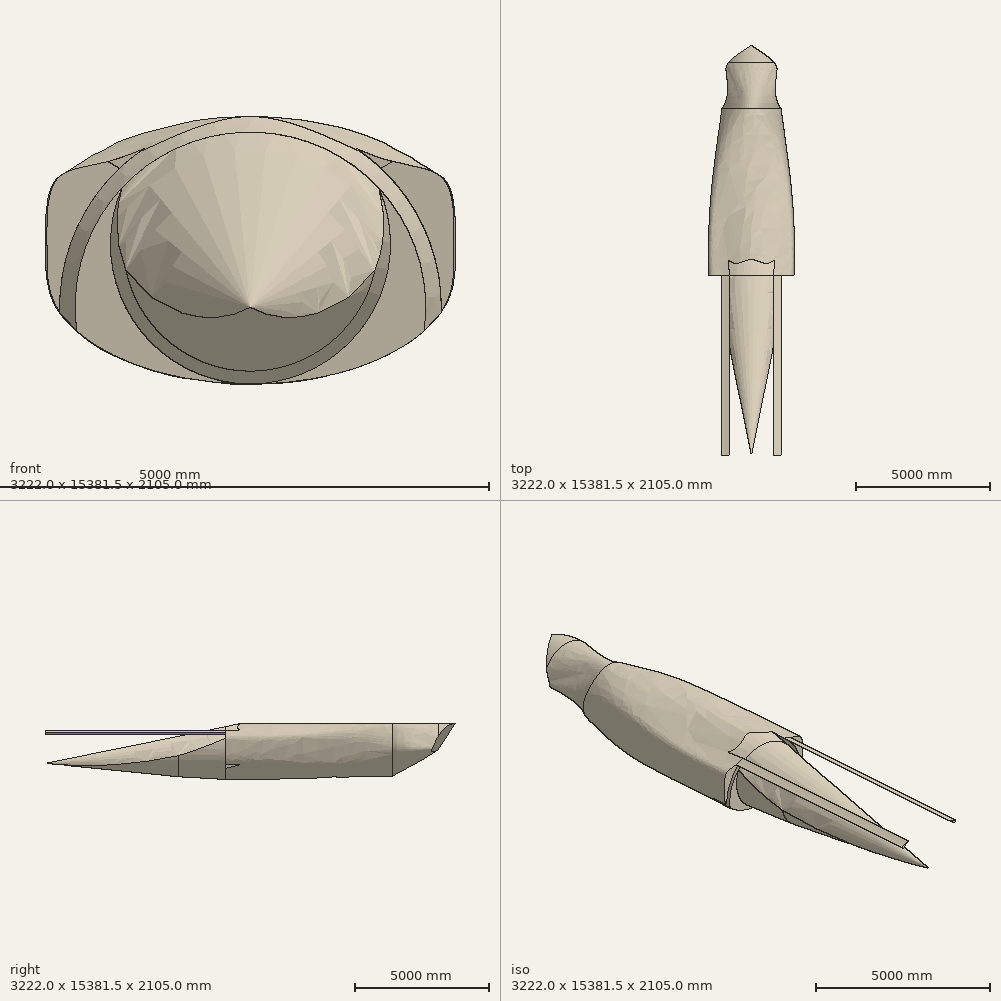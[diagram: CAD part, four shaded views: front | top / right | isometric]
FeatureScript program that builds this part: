
annotation { "Feature Type Name" : "Feature", "Feature Type Description" : "" }
export const myFeature = defineFeature(function(context is Context, id is Id, definition is map)
    precondition{}
    {
        {
            var Q0;
            Q0=qCreatedBy(makeId("Front.planeOp"),FACE);
            cPlane(context, id + "F0", {"entities" : qUnion([Q0]), "cplaneType" : CPlaneType.OFFSET, "offset" : 1750 * mm, "width" : 152.4 * mm, "height" : 152.4 * mm});
        }
        {
            var Q0;
            Q0=qCreatedBy(id+"F0.planeOp",FACE);
            var sketch = newSketch(context, id + "F1", { "sketchPlane" : qUnion([Q0])});
            skPoint(sketch, "E0.middle", {"position": v(0, 0) * mm});
            skFitSpline(sketch, "E1", {"points": [v(0, 1000) * mm, v(1060, 662.5) * mm, v(1517.6, 506.84) * mm, v(1600, 0) * mm, v(1517.6, -506.84) * mm, v(750, -1000) * mm, v(-750, -1000) * mm, v(-1517.6, -506.84) * mm, v(-1600, 0) * mm, v(-1517.6, 506.84) * mm, v(-1060, 662.5) * mm, v(0, 1000) * mm]});
            skSolve(sketch);
        }
        {
            var Q0;
            Q0=qCreatedBy(makeId("Front.planeOp"),FACE);
            var sketch = newSketch(context, id + "F2", { "sketchPlane" : qUnion([Q0])});
            skPoint(sketch, "E2.middle", {"position": v(0, 0) * mm});
            skFitSpline(sketch, "E3", {"points": [v(0, 1000) * mm, v(1060, 662.5) * mm, v(1517.6, 506.84) * mm, v(1600, 0) * mm, v(1517.6, -506.84) * mm, v(750, -1000) * mm, v(-750, -1000) * mm, v(-1517.6, -506.84) * mm, v(-1600, 0) * mm, v(-1517.6, 506.84) * mm, v(-1060, 662.5) * mm, v(0, 1000) * mm]});
            skSolve(sketch);
        }
        {
            var Q0;
            Q0=qCreatedBy(makeId("Front.planeOp"),FACE);
            cPlane(context, id + "F3", {"entities" : qUnion([Q0]), "cplaneType" : CPlaneType.OFFSET, "offset" : 3500 * mm, "oppositeDirection" : true, "width" : 150 * mm, "height" : 150 * mm});
        }
        {
            var Q0;
            Q0=qCreatedBy(id+"F3.planeOp",FACE);
            var sketch = newSketch(context, id + "F4", { "sketchPlane" : qUnion([Q0])});
            skPoint(sketch, "E4.middle", {"position": v(0, 0) * mm});
            skFitSpline(sketch, "E5", {"points": [v(0, 1000) * mm, v(1060, 662.5) * mm, v(1250, 0) * mm, v(1060, -662.5) * mm, v(0, -1000) * mm, v(-1060, -662.5) * mm, v(-1250, 0) * mm, v(-1060, 662.5) * mm, v(0, 1000) * mm]});
            skSolve(sketch);
        }
        {
            var Q0;
            Q0=qCreatedBy(makeId("Front.planeOp"),FACE);
            cPlane(context, id + "F5", {"entities" : qUnion([Q0]), "cplaneType" : CPlaneType.OFFSET, "offset" : 4500 * mm, "oppositeDirection" : true, "width" : 150 * mm, "height" : 150 * mm});
        }
        {
            var Q0;
            Q0=qCreatedBy(id+"F5.planeOp",FACE);
            var sketch = newSketch(context, id + "F6", { "sketchPlane" : qUnion([Q0])});
            skPoint(sketch, "E6.middle", {"position": v(0, 0) * mm});
            skFitSpline(sketch, "E7", {"points": [v(0, 1000) * mm, v(848, 530) * mm, v(1108.5, 0) * mm, v(848, -530) * mm, v(0, -1000) * mm, v(-848, -530) * mm, v(-1108.5, 0) * mm, v(-848, 530) * mm, v(0, 1000) * mm]});
            skSolve(sketch);
        }
        {
            var Q0;
            Q0=qCreatedBy(makeId("Front.planeOp"),FACE);
            cPlane(context, id + "F7", {"entities" : qUnion([Q0]), "cplaneType" : CPlaneType.OFFSET, "offset" : 6232.05 * mm, "oppositeDirection" : true, "width" : 150 * mm, "height" : 150 * mm});
        }
        {
            var Q0;
            Q0=qCreatedBy(id+"F7.planeOp",FACE);
            var sketch = newSketch(context, id + "F8", { "sketchPlane" : qUnion([Q0])});
            skArc(sketch, "E8", {"start": v(998.61, 52.63) * mm, "mid": v(0, 1000) * mm, "end": v(-998.61, 52.63) * mm});
            skLineSegment(sketch, "E9", {"start": v(0, 0) * mm, "end": v(-948.68, 0) * mm});
            skLineSegment(sketch, "E10", {"start": v(0, 0) * mm, "end": v(948.68, 0) * mm});
            skPoint(sketch, "E11.visualSharp", {"position": v(-1000, 0) * mm});
            skArc(sketch, "E11.filletArc", {"start": v(-998.61, 52.63) * mm, "mid": v(-984.96, 15.59) * mm, "end": v(-948.68, 0) * mm});
            skPoint(sketch, "E12.visualSharp", {"position": v(1000, 0) * mm});
            skArc(sketch, "E12.filletArc", {"start": v(948.68, 0) * mm, "mid": v(984.96, 15.59) * mm, "end": v(998.61, 52.63) * mm});
            skSolve(sketch);
        }
        {
            var Q0;
            Q0=sQuery(id+"F8.wireOp",EDGE,"E9");
            var Q1;
            Q1=sQuery(id+"F6.wireOp",VERTEX,"E7.6.internal");
            cPlane(context, id + "F9", {"entities" : qUnion([Q0, Q1]), "cplaneType" : CPlaneType.LINE_ANGLE, "offset" : 25 * mm, "angle" : 0 * degree, "width" : 150 * mm, "height" : 150 * mm});
        }
        {
            var Q0;
            Q0=qCreatedBy(id+"F9.planeOp",FACE);
            var sketch = newSketch(context, id + "F10", { "sketchPlane" : qUnion([Q0])});
            skFitSpline(sketch, "E13", {"points": [v(-1108.5, 4500) * mm, v(-948.68, 6232.05) * mm], "startDerivative": vector(1200, 1755) * mm, "endDerivative": vector(158.07, 1422.55) * mm});
            skFitSpline(sketch, "E14", {"points": [v(1108.5, 4500) * mm, v(948.68, 6232.05) * mm], "startDerivative": vector(-1200, 1755) * mm, "endDerivative": vector(-158.07, 1422.55) * mm});
            skSolve(sketch);
        }
        {
            var Q0;
            Q0=makeQuery(id+"F1.imprint","IMPRINT",FACE,{"disambiguationData":[TD([[makeQuery(id+"F1.imprint","IMPRINT",EDGE,{"derivedFrom":sQuery(id+"F1.wireOp",EDGE,"E1")}),-1.0]])]});
            var Q1;
            Q1=makeQuery(id+"F2.imprint","IMPRINT",FACE,{"disambiguationData":[TD([[makeQuery(id+"F2.imprint","IMPRINT",EDGE,{"derivedFrom":sQuery(id+"F2.wireOp",EDGE,"E3")}),-1.0]])]});
            var Q2;
            Q2=makeQuery(id+"F4.imprint","IMPRINT",FACE,{"disambiguationData":[TD([[makeQuery(id+"F4.imprint","IMPRINT",EDGE,{"derivedFrom":sQuery(id+"F4.wireOp",EDGE,"E5")}),-1.0]])]});
            var Q3;
            Q3=makeQuery(id+"F6.imprint","IMPRINT",FACE,{"disambiguationData":[TD([[makeQuery(id+"F6.imprint","IMPRINT",EDGE,{"derivedFrom":sQuery(id+"F6.wireOp",EDGE,"E7")}),-1.0]])]});
            loft(context, id + "F11", {"sheetProfilesArray" : [{ "sheetProfileEntities" : qUnion([Q0]) }, { "sheetProfileEntities" : qUnion([Q1]) }, { "sheetProfileEntities" : qUnion([Q2]) }, { "sheetProfileEntities" : qUnion([Q3]) }]});
        }
        {
            var Q1;
            Q1=makeQuery(id+"F6.imprint","IMPRINT",FACE,{"disambiguationData":[TD([[makeQuery(id+"F6.imprint","IMPRINT",EDGE,{"derivedFrom":sQuery(id+"F6.wireOp",EDGE,"E7")}),-1.0]])]});
            var Q2;
            Q2=makeQuery(id+"F8.imprint","IMPRINT",FACE,{"disambiguationData":[TD([[makeQuery(id+"F8.imprint","IMPRINT",EDGE,{"derivedFrom":sQuery(id+"F8.wireOp",EDGE,"E8")}),1.0]])]});
            var Q3;
            Q3=sQuery(id+"F10.wireOp",EDGE,"E13");
            var Q4;
            Q4=sQuery(id+"F10.wireOp",EDGE,"E14");
            loft(context, id + "F12", {"operationType" : NewBodyOperationType.ADD, "addGuides" : true, "sheetProfilesArray" : [{ "sheetProfileEntities" : qUnion([Q1]) }, { "sheetProfileEntities" : qUnion([Q2]) }], "guidesArray" : [{ "guideEntities" : qUnion([Q3]), "guideDerivativeType" : LoftGuideDerivativeType.DEFAULT, "guideDerivativeMagnitude" : 1 }, { "guideEntities" : qUnion([Q4]), "guideDerivativeType" : LoftGuideDerivativeType.DEFAULT, "guideDerivativeMagnitude" : 1 }]});
        }
        {
            var Q0;
            Q0=qSketchRegion(id+"F1",true);
            extrude(context, id + "F13", {"entities" : qUnion([Q0]), "depth" : 6750 * mm});
        }
        {
            var Q0;
            Q0=qCreatedBy(makeId("Right.planeOp"),FACE);
            var sketch = newSketch(context, id + "F14", { "sketchPlane" : qUnion([Q0])});
            skLineSegment(sketch, "E15", {"start": v(0, 0) * mm, "end": v(-3500, 0) * mm});
            skLineSegment(sketch, "E16", {"start": v(-3500, 0) * mm, "end": v(-3500, -1000) * mm});
            skLineSegment(sketch, "E17", {"start": v(-3500, -1000) * mm, "end": v(-8500, -1000) * mm});
            skLineSegment(sketch, "E18", {"start": v(-8500, -1000) * mm, "end": v(-8500, -499.31) * mm});
            skLineSegment(sketch, "E19", {"start": v(-1151.4, 0) * mm, "end": v(-1151.4, 1000) * mm});
            skLineSegment(sketch, "E20", {"start": v(-1151.4, 1000) * mm, "end": v(-8500, -499.31) * mm});
            skLineSegment(sketch, "E21", {"start": v(-8500, -499.31) * mm, "end": v(-3500, -1000) * mm});
            skLineSegment(sketch, "E22", {"start": v(-3500, 1000) * mm, "end": v(4500, 1000) * mm});
            skLineSegment(sketch, "E23", {"start": v(-3500, 1000) * mm, "end": v(-8500, 1000) * mm});
            skLineSegment(sketch, "E24", {"start": v(-8500, 1000) * mm, "end": v(-8500, -499.31) * mm});
            skLineSegment(sketch, "E25", {"start": v(-8500, -1000) * mm, "end": v(-8500, -1750) * mm});
            skLineSegment(sketch, "E26", {"start": v(-8500, -1750) * mm, "end": v(-1750, -1750) * mm});
            skPoint(sketch, "E26.endSnap0", {"position": v(-1750, 0) * mm});
            skLineSegment(sketch, "E27", {"start": v(-1750, 0) * mm, "end": v(-1750, -1099.92) * mm});
            skLineSegment(sketch, "E28", {"start": v(-1750, -1099.92) * mm, "end": v(-3500, -1000) * mm});
            skLineSegment(sketch, "E29", {"start": v(-1750, -1099.92) * mm, "end": v(-1750, -1750) * mm});
            skLineSegment(sketch, "E30", {"start": v(-8500, -499.31) * mm, "end": v(-3500, -499.31) * mm});
            skSolve(sketch);
        }
        {
            var Q0;
            {var subQ0=sQuery(id+"F14.wireOp",EDGE,"E20");Q0=makeQuery(id+"F14.imprint","IMPRINT",FACE,{"disambiguationData":[TD([[makeQuery(id+"F14.imprint","IMPRINT",EDGE,{"derivedFrom":subQ0}),-1.0]])]});}
            var Q1;
            Q1=sQuery(id+"F14.wireOp",EDGE,"E30");
            revolve(context, id + "F15", {"operationType" : NewBodyOperationType.REMOVE, "entities" : qUnion([Q0]), "axis" : qUnion([Q1]), "revolveType" : RevolveType.SYMMETRIC, "oppositeDirection" : true, "angle" : 250 * degree});
        }
        {
            var Q0;
            Q0=makeQuery(id+"F14.imprint","IMPRINT",FACE,{"disambiguationData":[TD([[makeQuery(id+"F14.imprint","IMPRINT",EDGE,{"derivedFrom":sQuery(id+"F14.wireOp",EDGE,"E17")}),-1.0]])]});
            var Q1;
            Q1=makeQuery(id+"F14.imprint","IMPRINT",FACE,{"disambiguationData":[TD([[makeQuery(id+"F14.imprint","IMPRINT",EDGE,{"derivedFrom":sQuery(id+"F14.wireOp",EDGE,"E17")}),1.0]])]});
            var Q2;
            Q2=sQuery(id+"F14.wireOp",EDGE,"E15");
            revolve(context, id + "F16", {"operationType" : NewBodyOperationType.REMOVE, "entities" : qUnion([Q0, Q1]), "axis" : qUnion([Q2]), "revolveType" : RevolveType.SYMMETRIC, "oppositeDirection" : true, "angle" : 240 * degree});
        }
        {
            var Q0;
            Q0=makeQuery(id+"F12.opLoft","CAP_FACE",FACE,{"disambiguationData":[OSD([makeQuery(id+"F8.imprint","IMPRINT",FACE,{"disambiguationData":[TD([[makeQuery(id+"F8.imprint","IMPRINT",EDGE,{"derivedFrom":sQuery(id+"F8.wireOp",EDGE,"E8")}),1.0]])]})])],"isStart":true});
            extrude(context, id + "F17", {"entities" : qUnion([Q0]), "operationType" : NewBodyOperationType.ADD, "depth" : 649.4 * mm});
        }
        {
            var Q0;
            Q0=qCreatedBy(makeId("Right.planeOp"),FACE);
            var sketch = newSketch(context, id + "F18", { "sketchPlane" : qUnion([Q0])});
            skLineSegment(sketch, "E31", {"start": v(0, 0) * mm, "end": v(4500, 0) * mm});
            skLineSegment(sketch, "E32", {"start": v(4500, 0) * mm, "end": v(6232.05, 0) * mm});
            skLineSegment(sketch, "E33", {"start": v(4500, 0) * mm, "end": v(4500, 1000) * mm});
            skLineSegment(sketch, "E34", {"start": v(4500, 1000) * mm, "end": v(6881.46, 1000) * mm});
            skLineSegment(sketch, "E35", {"start": v(6881.46, 1000) * mm, "end": v(6881.46, -1000) * mm});
            skLineSegment(sketch, "E36", {"start": v(6881.46, 1000) * mm, "end": v(6232.05, 0) * mm});
            skLineSegment(sketch, "E37", {"start": v(6232.05, 0) * mm, "end": v(5582.64, -1000) * mm});
            skLineSegment(sketch, "E38", {"start": v(5582.64, -1000) * mm, "end": v(6881.46, -1000) * mm});
            skSolve(sketch);
        }
        {
            var Q0;
            Q0=makeQuery(id+"F18.imprint","IMPRINT",FACE,{"disambiguationData":[TD([[makeQuery(id+"F18.imprint","IMPRINT",EDGE,{"derivedFrom":sQuery(id+"F18.wireOp",EDGE,"E35")}),-1.0]])]});
            var Q1;
            Q1=sQuery(id+"F18.wireOp",EDGE,"E34");
            revolve(context, id + "F19", {"operationType" : NewBodyOperationType.REMOVE, "entities" : qUnion([Q0]), "axis" : qUnion([Q1]), "revolveType" : RevolveType.SYMMETRIC, "oppositeDirection" : true, "angle" : 182 * degree});
        }
    });
